# Revit family: LAMP_FIL 45 1680MM OPAL RECESSED
name_source: partatom
category: Luminarias
revit_build: Autodesk Revit 2018 (Build: 20170223_1515(x64)
units: mm (PartAtom-declared; Revit-internal decimal feet)

## family parameters
Anfitrión = Cara
Compartido = No
Corte con vacíos al cargar = No
Cota de conector redondo = Diámetro de uso
Origen de luz = Sí
Punto de cálculo de habitación = No
Tipo de pieza = Normal

## types (24) — shared parameters
CRI = 80
Cambio de temperatura de color de luz atenuada = <Ninguno>
Dimensions = 1680x55x76
Elevación por defecto = 1219 mm
Fabricante = LAMP
Filtro de color = 16777215
Gear = Electronic
IEE = A+
Installation instructions = https://www.lamp.es
Insulation class = I
Lamp = MID-POWER LED
Last update = 25/03/2021
Longitud de línea de emisión = 1680 mm  [stored 5.51181 ft]
MacAdam = 3
Manufacturer URL = http://www.lamp.es
Manufacturer country = Spain
Manufacturer name = LAMP
Material difusor = LAMP_PC Difusor Opal Fil
Material suspension = LAMP_Acero genérico
Power Supply = 220-240V 50/60Hz
Product URL = https://www.lamp.es
Product datasheet = http://www.lamp.es
Protection rating = IP20 / IK07
Recessed dimensions = 1686x55x76
Type = MID POWER TRIDONIC
Ángulo de inclinación = -90.00°

## per-type parameters (varying)
| type | Archivo de red fotométrica | Descripción | Efficacy | Finish | LED Lifetime | Material perfil | Modelo | Plum | Power | Product code | Weight |
| 3900LM 3000K DALI BLACK | F41RE168MOOP830nB.IES | FIL45 REC 1680 3900 WW OPAL DALI BK. | 105 lm/W | Matte black RAL 9011 | 70.000 L80 B10 | LAMP_Aluminio Perfil Fil NG | F41RE168MOOP830DB | 25 W | 23 W | F41RE168MOOP830DB | 3.92 kg |
| 3900LM 3000K DALI GREY | F41RE168MOOP830nG.IES | FIL45 REC 1680 3900 WW OPAL DALI GR. | 105 lm/W | Gloss grey | 70.000 L80 B10 | LAMP_Aluminio Perfil Fil GR | F41RE168MOOP830DG | 25 W | 23 W | F41RE168MOOP830DG | 3.92 kg |
| 3900LM 3000K DALI WHITE | F41RE168MOOP830nW.IES | FIL45 REC 1680 3900 WW OPAL DALI WH. | 105 lm/W | Matte white RAL 9010 | 70.000 L80 B10 | LAMP_Aluminio Perfil Fil BL | F41RE168MOOP830DW | 25 W | 23 W | F41RE168MOOP830DW | 3.92 kg |
| 3900LM 3000K  BLACK | F41RE168MOOP830NB.IES | FIL45 REC 1680 3900 WW OPAL BK. | 105 lm/W | Matte black RAL 9011 | 70.000 L80 B10 | LAMP_Aluminio Perfil Fil NG | F41RE168MOOP830NB | 25 W | 23 W | F41RE168MOOP830NB | 3.72 kg |
| 3900LM 3000K  GREY | F41RE168MOOP830NG.IES | FIL45 REC 1680 3900 WW OPAL GR. | 105 lm/W | Gloss grey | 70.000 L80 B10 | LAMP_Aluminio Perfil Fil GR | F41RE168MOOP830NG | 25 W | 23 W | F41RE168MOOP830NG | 3.72 kg |
| 3900LM 3000K  WHITE | F41RE168MOOP830NW.IES | FIL45 REC 1680 3900 WW OPAL WH. | 105 lm/W | Matte white RAL 9010 | 70.000 L80 B10 | LAMP_Aluminio Perfil Fil BL | F41RE168MOOP830NW | 25 W | 23 W | F41RE168MOOP830NW | 3.72 kg |
| 3900LM 4000K DALI BLACK | F41RE168MOOP840nB.IES | FIL45 REC 1680 3900 NW OPAL DALI BK. | 110 lm/W | Matte black RAL 9011 | 70.000 L80 B10 | LAMP_Aluminio Perfil Fil NG | F41RE168MOOP840DB | 25 W | 23 W | F41RE168MOOP840DB | 3.92 kg |
| 3900LM 4000K DALI GREY | F41RE168MOOP840nG.IES | FIL45 REC 1680 3900 NW OPAL DALI GR. | 110 lm/W | Gloss grey | 70.000 L80 B10 | LAMP_Aluminio Perfil Fil GR | F41RE168MOOP840DG | 25 W | 23 W | F41RE168MOOP840DG | 3.92 kg |
| 3900LM 4000K DALI WHITE | F41RE168MOOP840nW.IES | FIL45 REC 1680 3900 NW OPAL DALI WH. | 110 lm/W | Matte white RAL 9010 | 70.000 L80 B10 | LAMP_Aluminio Perfil Fil BL | F41RE168MOOP840DW | 25 W | 23 W | F41RE168MOOP840DW | 3.92 kg |
| 3900LM 4000K  BLACK | F41RE168MOOP840NB.IES | FIL45 REC 1680 3900 NW OPAL BK. | 110 lm/W | Matte black RAL 9011 | 70.000 L80 B10 | LAMP_Aluminio Perfil Fil NG | F41RE168MOOP840NB | 25 W | 23 W | F41RE168MOOP840NB | 3.72 kg |
| 3900LM 4000K  GREY | F41RE168MOOP840NG.IES | FIL45 REC 1680 3900 NW OPAL GR. | 110 lm/W | Gloss grey | 70.000 L80 B10 | LAMP_Aluminio Perfil Fil GR | F41RE168MOOP840NG | 25 W | 23 W | F41RE168MOOP840NG | 3.72 kg |
| 3900LM 4000K  WHITE | F41RE168MOOP840NW.IES | FIL45 REC 1680 3900 NW OPAL WH. | 110 lm/W | Matte white RAL 9010 | 70.000 L80 B10 | LAMP_Aluminio Perfil Fil BL | F41RE168MOOP840NW | 25 W | 23 W | F41RE168MOOP840NW | 3.72 kg |
| 9300LM 3000K DALI BLACK | F41RE168HOOP830nB.IES | FIL45 REC 1680 9300 WW OPAL DALI BK. | 95 lm/W | Matte black RAL 9011 | 72.000 L80 B10 | LAMP_Aluminio Perfil Fil NG | F41RE168HOOP830DB | 59 W | 54 W | F41RE168HOOP830DB | 3.94 kg |
| 9300LM 3000K DALI GREY | F41RE168HOOP830nG.IES | FIL45 REC 1680 9300 WW OPAL DALI BK. | 95 lm/W | Gloss grey | 72.000 L80 B10 | LAMP_Aluminio Perfil Fil GR | F41RE168HOOP830DG | 59 W | 54 W | F41RE168HOOP830DG | 3.94 kg |
| 9300LM 3000K DALI WHITE | F41RE168HOOP830nW.IES | FIL45 REC 1680 9300 WW OPAL DALI GR. | 95 lm/W | Matte white RAL 9010 | 72.000 L80 B10 | LAMP_Aluminio Perfil Fil BL | F41RE168HOOP830DW | 59 W | 54 W | F41RE168HOOP830DW | 3.94 kg |
| 9300LM 3000K  BLACK | F41RE168HOOP830NB.IES | FIL45 REC 1680 9300 WW OPAL BK. | 95 lm/W | Matte black RAL 9011 | 72.000 L80 B10 | LAMP_Aluminio Perfil Fil NG | F41RE168HOOP830NB | 59 W | 54 W | F41RE168HOOP830NB | 3.77 kg |
| 9300LM 3000K  GREY | F41RE168HOOP830NG.IES | FIL45 REC 1680 9300 WW OPAL GR. | 95 lm/W | Gloss grey | 72.000 L80 B10 | LAMP_Aluminio Perfil Fil GR | F41RE168HOOP830NG | 59 W | 54 W | F41RE168HOOP830NG | 3.77 kg |
| 9300LM 3000K  WHITE | F41RE168HOOP830NW.IES | FIL45 REC 1680 9300 WW OPAL WH. | 95 lm/W | Matte white RAL 9010 | 72.000 L80 B10 | LAMP_Aluminio Perfil Fil BL | F41RE168HOOP830NW | 59 W | 54 W | F41RE168HOOP830NW | 3.77 kg |
| 9300LM 4000K DALI BLACK | F41RE168HOOP840nB.IES | FIL45 REC 1680 9300 NW OPAL DALI BK. | 95 lm/W | Matte black RAL 9011 | 72.000 L80 B10 | LAMP_Aluminio Perfil Fil NG | F41RE168HOOP840DB | 59 W | 54 W | F41RE168HOOP840DB | 3.94 kg |
| 9300LM 4000K DALI GREY | F41RE168HOOP840nG.IES | FIL45 REC 1680 9300 NW OPAL DALI GR. | 95 lm/W | Gloss grey | 72.000 L80 B10 | LAMP_Aluminio Perfil Fil GR | F41RE168HOOP840DG | 59 W | 54 W | F41RE168HOOP840DG | 3.94 kg |
| 9300LM 4000K DALI WHITE | F41RE168HOOP840nW.IES | FIL45 REC 1680 9300 NW OPAL DALI WH. | 95 lm/W | Matte white RAL 9010 | 72.000 L80 B10 | LAMP_Aluminio Perfil Fil BL | F41RE168HOOP840DW | 59 W | 54 W | F41RE168HOOP840DW | 3.94 kg |
| 9300LM 4000K  BLACK | F41RE168HOOP840NB.IES | FIL45 REC 1680 9300 NW OPAL BK. | 95 lm/W | Matte black RAL 9011 | 72.000 L80 B10 | LAMP_Aluminio Perfil Fil NG | F41RE168HOOP840NB | 59 W | 54 W | F41RE168HOOP840NB | 3.77 kg |
| 9300LM 4000K  GREY | F41RE168HOOP840NG.IES | FIL45 REC 1680 9300 NW OPAL GR. | 95 lm/W | Gloss grey | 72.000 L80 B10 | LAMP_Aluminio Perfil Fil GR | F41RE168HOOP840NG | 59 W | 54 W | F41RE168HOOP840NG | 3.77 kg |
| 9300LM 4000K  WHITE | F41RE168HOOP840NW.IES | FIL45 REC 1680 9300 NW OPAL WH. | 95 lm/W | Matte white RAL 9010 | 72.000 L80 B10 | LAMP_Aluminio Perfil Fil BL | F41RE168HOOP840NW | 59 W | 54 W | F41RE168HOOP840NW | 3.77 kg |

note: [stored X ft] marks values corroborated as IEEE doubles in the binary element streams (Revit-internal decimal feet)
